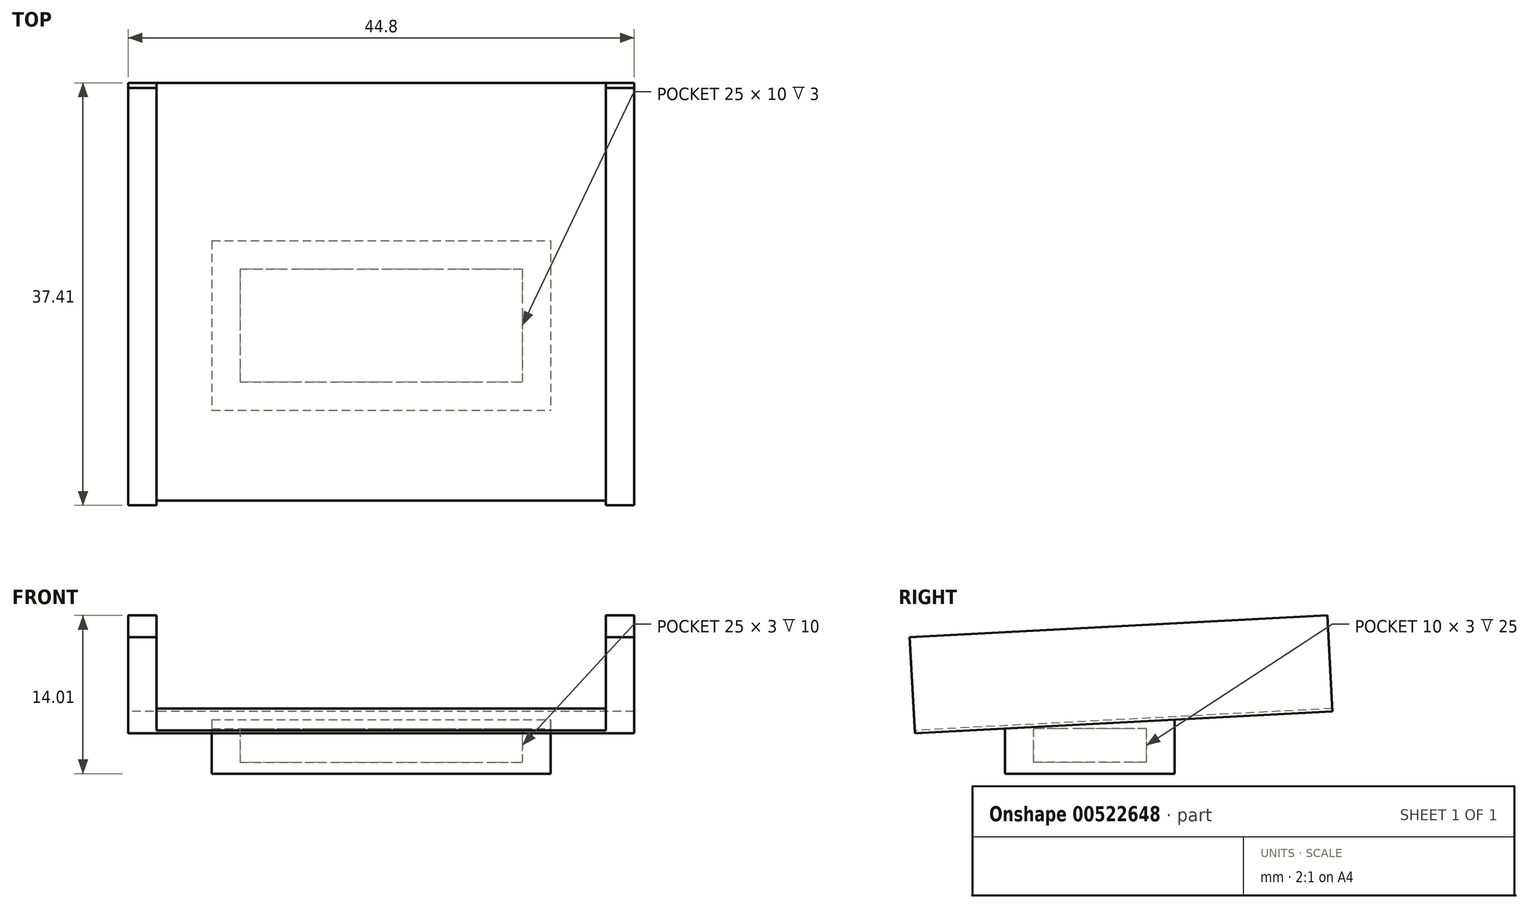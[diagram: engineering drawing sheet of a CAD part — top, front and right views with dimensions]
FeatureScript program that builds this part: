
annotation { "Feature Type Name" : "Feature", "Feature Type Description" : "" }
export const myFeature = defineFeature(function(context is Context, id is Id, definition is map)
    precondition{}
    {
        {
            assignVariable(context, id + "F0", {"name" : "thick", "anyValue" : 0.25});
        }
        {
            var Q0;
            Q0=qCreatedBy(makeId("Top.planeOp"),FACE);
            var sketch = newSketch(context, id + "F1", { "sketchPlane" : qUnion([Q0])});
            skLineSegment(sketch, "E0.bottom", {"start": v(-15, 7.5) * mm, "end": v(15, 7.5) * mm});
            skLineSegment(sketch, "E0.top", {"start": v(-15, -7.5) * mm, "end": v(15, -7.5) * mm});
            skLineSegment(sketch, "E0.left", {"start": v(-15, 7.5) * mm, "end": v(-15, -7.5) * mm});
            skLineSegment(sketch, "E0.right", {"start": v(15, 7.5) * mm, "end": v(15, -7.5) * mm});
            skLineSegment(sketch, "E1.bottom", {"start": v(-12.5, 5) * mm, "end": v(12.5, 5) * mm});
            skLineSegment(sketch, "E1.top", {"start": v(-12.5, -5) * mm, "end": v(12.5, -5) * mm});
            skLineSegment(sketch, "E1.left", {"start": v(-12.5, 5) * mm, "end": v(-12.5, -5) * mm});
            skLineSegment(sketch, "E1.right", {"start": v(12.5, 5) * mm, "end": v(12.5, -5) * mm});
            skLineSegment(sketch, "E2", {"start": v(0, 7.5) * mm, "end": v(0, -7.5) * mm, "construction": true});
            skLineSegment(sketch, "E3", {"start": v(15, 0) * mm, "end": v(-15, 0) * mm, "construction": true});
            skSolve(sketch);
        }
        {
            var Q0;
            Q0=makeQuery(id+"F1.imprint","IMPRINT",FACE,{"disambiguationData":[TD([[makeQuery(id+"F1.imprint","IMPRINT",EDGE,{"derivedFrom":sQuery(id+"F1.wireOp",EDGE,"E0.bottom")}),-1.0]])]});
            extrude(context, id + "F2", {"entities" : qUnion([Q0]), "depth" : 3 * mm, "offsetDistance" : 25 * mm});
        }
        {
            var Q0;
            Q0=makeQuery(id+"F1.imprint","IMPRINT",FACE,{"disambiguationData":[TD([[makeQuery(id+"F1.imprint","IMPRINT",EDGE,{"derivedFrom":sQuery(id+"F1.wireOp",EDGE,"E1.bottom")}),-1.0]])]});
            var Q1;
            Q1=makeQuery(id+"F1.imprint","IMPRINT",FACE,{"disambiguationData":[TD([[makeQuery(id+"F1.imprint","IMPRINT",EDGE,{"derivedFrom":sQuery(id+"F1.wireOp",EDGE,"E0.bottom")}),-1.0]])]});
            extrude(context, id + "F3", {"entities" : qUnion([Q0, Q1]), "operationType" : NewBodyOperationType.ADD, "oppositeDirection" : true, "depth" : 1 * mm, "offsetDistance" : 25 * mm});
        }
        {
            var Q0;
            {var subQ0=sQuery(id+"F1.wireOp",EDGE,"E0.right");Q0=makeQuery(id+"F3.boolean.opBoolean","MERGE",FACE,{"derivedFrom":[makeQuery(id+"F2.opExtrude","SWEPT_FACE",FACE,{"disambiguationData":[OSD([subQ0])]}),makeQuery(id+"F3.opExtrude","SWEPT_FACE",FACE,{"disambiguationData":[OSD([subQ0])]})]});}
            var sketch = newSketch(context, id + "F4", { "sketchPlane" : qUnion([Q0])});
            skLineSegment(sketch, "E4.0.0", {"start": v(-7.5, 3) * mm, "end": v(-7.5, -1) * mm});
            skLineSegment(sketch, "E4.0.1", {"start": v(-7.5, -1) * mm, "end": v(7.5, -1) * mm});
            skLineSegment(sketch, "E4.0.2", {"start": v(7.5, -1) * mm, "end": v(7.5, 3) * mm});
            skLineSegment(sketch, "E4.0.3", {"start": v(7.5, 3) * mm, "end": v(-7.5, 3) * mm});
            skLineSegment(sketch, "E5", {"start": v(-7.5, 3) * mm, "end": v(7.5, 3.79) * mm});
            skLineSegment(sketch, "E6", {"start": v(7.5, 3.79) * mm, "end": v(7.5, 3) * mm});
            skSolve(sketch);
        }
        {
            var Q0;
            Q0=makeQuery(id+"F4.imprint","IMPRINT",FACE,{"disambiguationData":[TD([[makeQuery(id+"F4.imprint","IMPRINT",EDGE,{"derivedFrom":sQuery(id+"F4.wireOp",EDGE,"E4.0.3")}),-1.0]])]});
            var Q1;
            {var subQ0=sQuery(id+"F1.wireOp",EDGE,"E0.left");Q1=makeQuery(id+"F3.boolean.opBoolean","MERGE",FACE,{"derivedFrom":[makeQuery(id+"F2.opExtrude","SWEPT_FACE",FACE,{"disambiguationData":[OSD([subQ0])]}),makeQuery(id+"F3.opExtrude","SWEPT_FACE",FACE,{"disambiguationData":[OSD([subQ0])]})]});}
            extrude(context, id + "F5", {"entities" : qUnion([Q0]), "operationType" : NewBodyOperationType.ADD, "endBound" : BoundingType.UP_TO_SURFACE, "oppositeDirection" : true, "depth" : 25 * mm, "endBoundEntityFace" : qUnion([Q1]), "offsetDistance" : 25 * mm});
        }
        {
            var Q0;
            Q0=makeQuery(id+"F5.opExtrude","SWEPT_FACE",FACE,{"disambiguationData":[OSD([sQuery(id+"F4.wireOp",EDGE,"E5")])]});
            var sketch = newSketch(context, id + "F6", { "sketchPlane" : qUnion([Q0])});
            skLineSegment(sketch, "E7.bottom", {"start": v(22.4, -15.33) * mm, "end": v(-22.4, -15.33) * mm});
            skLineSegment(sketch, "E7.top", {"start": v(22.4, 21.69) * mm, "end": v(-22.4, 21.69) * mm});
            skLineSegment(sketch, "E7.left", {"start": v(22.4, -15.33) * mm, "end": v(22.4, 21.69) * mm});
            skLineSegment(sketch, "E7.right", {"start": v(-22.4, -15.33) * mm, "end": v(-22.4, 21.69) * mm});
            skLineSegment(sketch, "E8", {"start": v(0, -15.33) * mm, "end": v(0, 21.69) * mm, "construction": true});
            skLineSegment(sketch, "E9", {"start": v(-19.9, -15.33) * mm, "end": v(-19.9, 21.69) * mm});
            skLineSegment(sketch, "E10.MirrorCS", {"start": v(19.9, -15.33) * mm, "end": v(19.9, 21.69) * mm});
            skLineSegment(sketch, "E11.0.0", {"start": v(15, 7.69) * mm, "end": v(-15, 7.69) * mm});
            skLineSegment(sketch, "E11.0.1", {"start": v(-15, 7.69) * mm, "end": v(-15, -7.33) * mm});
            skLineSegment(sketch, "E11.0.2", {"start": v(-15, -7.33) * mm, "end": v(15, -7.33) * mm});
            skLineSegment(sketch, "E11.0.3", {"start": v(15, -7.33) * mm, "end": v(15, 7.69) * mm});
            skSolve(sketch);
        }
        {
            var Q0;
            {var subQ0=sQuery(id+"F6.wireOp",EDGE,"E7.right");Q0=makeQuery(id+"F6.imprint","IMPRINT",FACE,{"disambiguationData":[TD([[makeQuery(id+"F6.imprint","IMPRINT",EDGE,{"derivedFrom":subQ0}),-1.0]])]});}
            var Q1;
            Q1=makeQuery(id+"F6.imprint","IMPRINT",FACE,{"disambiguationData":[TD([[makeQuery(id+"F6.imprint","IMPRINT",EDGE,{"derivedFrom":sQuery(id+"F6.wireOp",EDGE,"eb016045-6bcc-4fb3-8d9d-79252571f3ca.0.0")}),1.0]])]});
            var Q2;
            {var subQ0=sQuery(id+"F6.wireOp",EDGE,"E7.left");Q2=makeQuery(id+"F6.imprint","IMPRINT",FACE,{"disambiguationData":[TD([[makeQuery(id+"F6.imprint","IMPRINT",EDGE,{"derivedFrom":subQ0}),1.0]])]});}
            var Q3;
            Q3=makeQuery(id+"F6.imprint","IMPRINT",FACE,{"disambiguationData":[TD([[makeQuery(id+"F6.imprint","IMPRINT",EDGE,{"derivedFrom":sQuery(id+"F6.wireOp",EDGE,"eb016045-6bcc-4fb3-8d9d-79252571f3ca.0.0")}),-1.0]])]});
            var Q4;
            {var subQ0=sQuery(id+"F6.wireOp",EDGE,"E9");Q4=makeQuery(id+"F6.imprint","IMPRINT",FACE,{"disambiguationData":[TD([[makeQuery(id+"F6.imprint","IMPRINT",EDGE,{"derivedFrom":subQ0}),-1.0]])]});}
            var Q5;
            Q5=makeQuery(id+"F6.imprint","IMPRINT",FACE,{"disambiguationData":[TD([[makeQuery(id+"F6.imprint","IMPRINT",EDGE,{"derivedFrom":sQuery(id+"F6.wireOp",EDGE,"E11.0.0")}),-1.0]])]});
            extrude(context, id + "F7", {"entities" : qUnion([Q0, Q1, Q2, Q3, Q4, Q5]), "operationType" : NewBodyOperationType.ADD, "depth" : (getVariable(context, 'thick')) * mm, "offsetDistance" : 25 * mm});
        }
        {
            var Q0;
            {var subQ0=sQuery(id+"F6.wireOp",EDGE,"E7.right");Q0=makeQuery(id+"F6.imprint","IMPRINT",FACE,{"disambiguationData":[TD([[makeQuery(id+"F6.imprint","IMPRINT",EDGE,{"derivedFrom":subQ0}),-1.0]])]});}
            var Q1;
            {var subQ0=sQuery(id+"F6.wireOp",EDGE,"E7.left");Q1=makeQuery(id+"F6.imprint","IMPRINT",FACE,{"disambiguationData":[TD([[makeQuery(id+"F6.imprint","IMPRINT",EDGE,{"derivedFrom":subQ0}),1.0]])]});}
            extrude(context, id + "F8", {"entities" : qUnion([Q0, Q1]), "operationType" : NewBodyOperationType.ADD, "depth" : 8.5 * mm, "offsetDistance" : 25 * mm});
        }
    });
